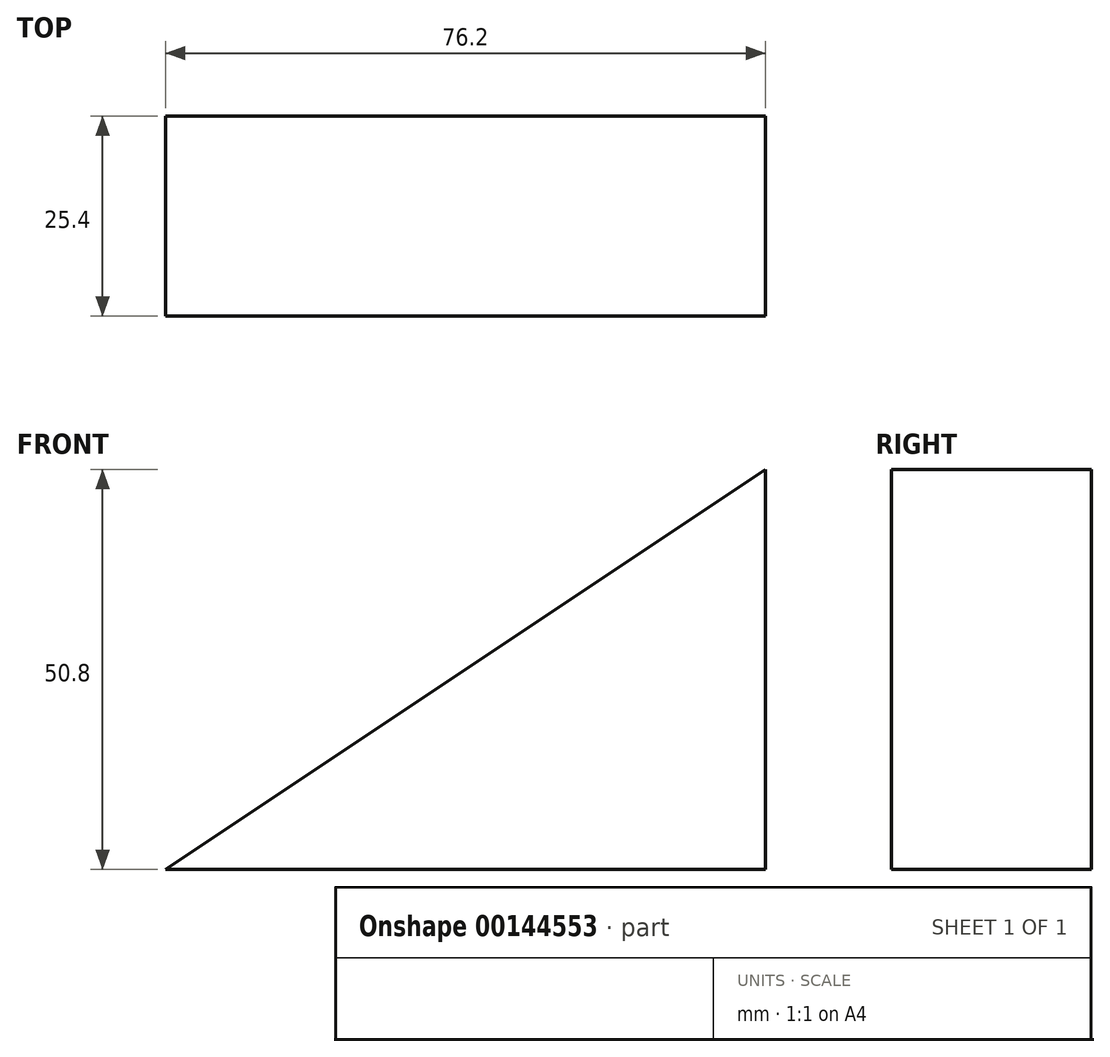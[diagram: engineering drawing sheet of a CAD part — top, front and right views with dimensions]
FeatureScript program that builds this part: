
annotation { "Feature Type Name" : "Feature", "Feature Type Description" : "" }
export const myFeature = defineFeature(function(context is Context, id is Id, definition is map)
    precondition{}
    {
        {
            var Q0;
            Q0=qCreatedBy(makeId("Front.planeOp"),FACE);
            var sketch = newSketch(context, id + "F0", { "sketchPlane" : qUnion([Q0])});
            skLineSegment(sketch, "E0", {"start": v(0, 0) * mm, "end": v(76.2, 0) * mm});
            skLineSegment(sketch, "E1", {"start": v(76.2, 0) * mm, "end": v(76.2, 50.8) * mm});
            skLineSegment(sketch, "E2", {"start": v(76.2, 50.8) * mm, "end": v(0, 0) * mm});
            skSolve(sketch);
        }
        {
            var Q0;
            Q0 = qSketchRegion(id + "F0", true);
            extrude(context, id + "F1", {"entities" : qUnion([Q0]), "depth" : 25.4 * mm});
        }
    });
